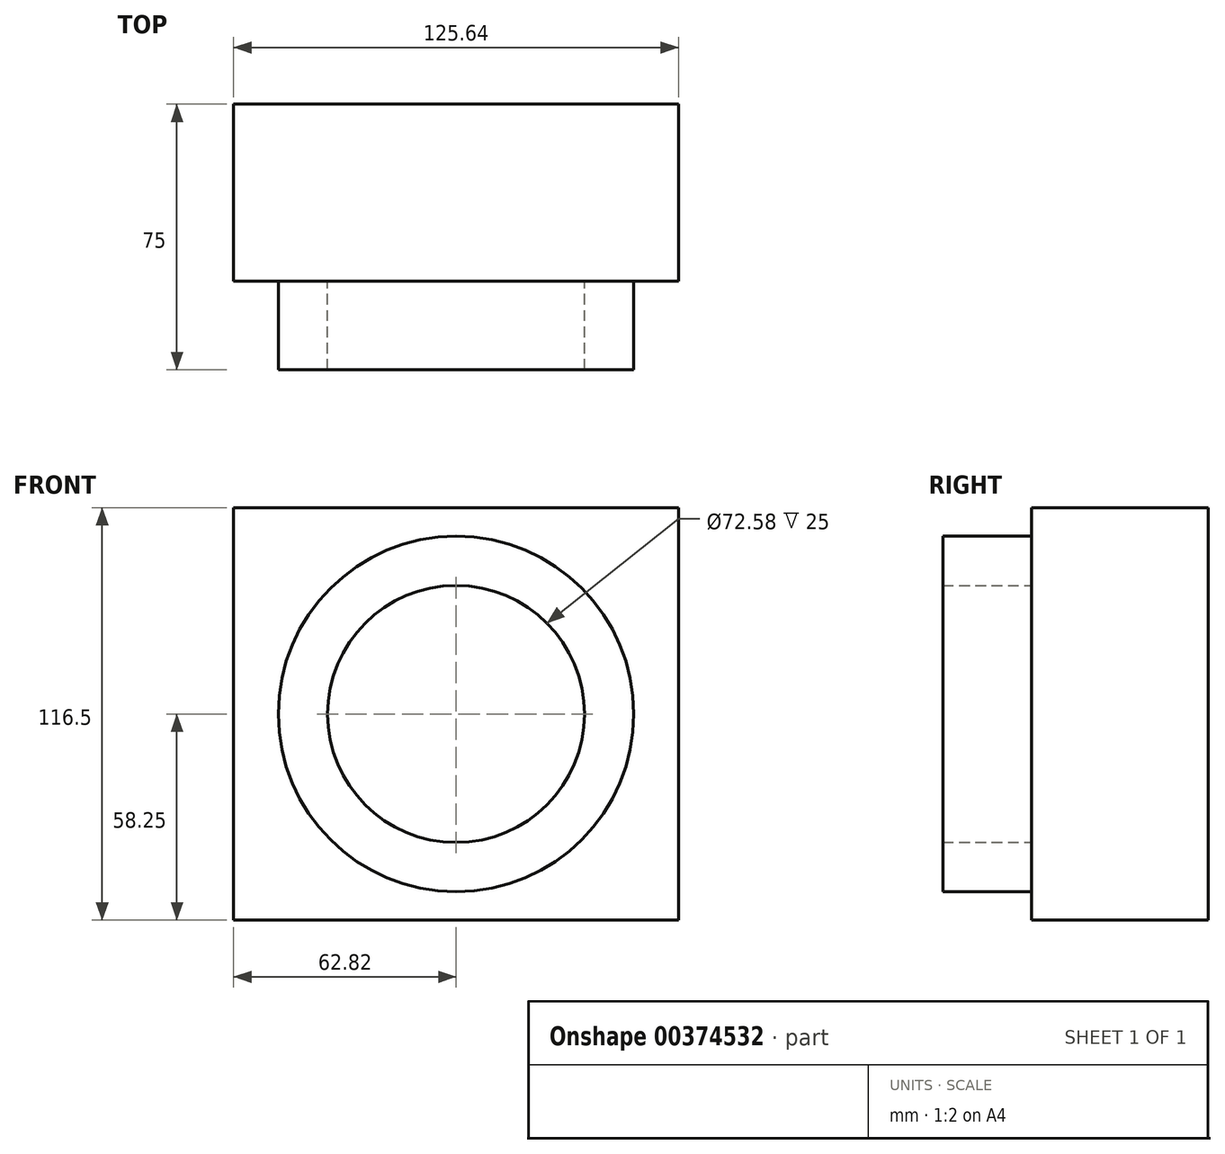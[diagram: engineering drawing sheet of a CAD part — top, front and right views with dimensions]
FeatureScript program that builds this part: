
annotation { "Feature Type Name" : "Feature", "Feature Type Description" : "" }
export const myFeature = defineFeature(function(context is Context, id is Id, definition is map)
    precondition{}
    {
        {
            var Q0;
            Q0=qCreatedBy(makeId("Front.planeOp"),FACE);
            var sketch = newSketch(context, id + "F0", { "sketchPlane" : qUnion([Q0])});
            skLineSegment(sketch, "E0.bottom", {"start": v(62.82, -58.25) * mm, "end": v(-62.82, -58.25) * mm});
            skLineSegment(sketch, "E0.top", {"start": v(62.82, 58.25) * mm, "end": v(-62.82, 58.25) * mm});
            skLineSegment(sketch, "E0.left", {"start": v(62.82, -58.25) * mm, "end": v(62.82, 58.25) * mm});
            skLineSegment(sketch, "E0.right", {"start": v(-62.82, -58.25) * mm, "end": v(-62.82, 58.25) * mm});
            skPoint(sketch, "E0.middle", {"position": v(0, 0) * mm});
            skSolve(sketch);
        }
        {
            var Q0;
            Q0=makeQuery(id+"F0.imprint","IMPRINT",FACE,{"disambiguationData":[TD([[makeQuery(id+"F0.imprint","IMPRINT",EDGE,{"derivedFrom":sQuery(id+"F0.wireOp",EDGE,"E0.bottom")}),-1.0]])]});
            extrude(context, id + "F1", {"entities" : qUnion([Q0]), "depth" : 50 * mm});
        }
        {
            var Q0;
            Q0=makeQuery(id+"F1.opExtrude","CAP_FACE",FACE,{"disambiguationData":[OSD([sQuery(id+"F0.wireOp",EDGE,"E0.bottom"),sQuery(id+"F0.wireOp",EDGE,"E0.top"),sQuery(id+"F0.wireOp",EDGE,"E0.left"),sQuery(id+"F0.wireOp",EDGE,"E0.right")])],"isStart":false});
            var sketch = newSketch(context, id + "F2", { "sketchPlane" : qUnion([Q0])});
            skCircle(sketch, "E1", {"center": v(0, 0) * mm, "radius": 50.2 * mm});
            skCircle(sketch, "E2", {"center": v(0, 0) * mm, "radius": 36.3 * mm});
            skSolve(sketch);
        }
        {
            var Q0;
            Q0=makeQuery(id+"F2.imprint","IMPRINT",FACE,{"disambiguationData":[TD([[makeQuery(id+"F2.imprint","IMPRINT",EDGE,{"derivedFrom":sQuery(id+"F2.wireOp",EDGE,"E1")}),1.0]])]});
            extrude(context, id + "F3", {"entities" : qUnion([Q0]), "operationType" : NewBodyOperationType.ADD, "depth" : 25 * mm});
        }
    });
